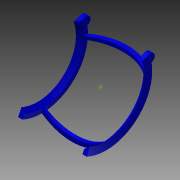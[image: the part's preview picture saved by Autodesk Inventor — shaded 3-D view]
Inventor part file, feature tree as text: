
AUTODESK INVENTOR PART (.ipt)
format: ipt  version: 2014 (Build 180170000, 170)  size: 196,608 bytes
history: native  units: in
note: dims shown in document units (in); Inventor stores cm internally (conversion verified against a paired STEP export)
features: sketch x8, revolve x4, extrude x3, plane x2, projected_geometry x2
ambient origin geometry x8: Origin, YZ Plane, XZ Plane, XY Plane, X Axis, Y Axis, Z Axis, Center Point
bodies: Solid1 (feature_tree)
feature tree (19):
  sketch  "Sketch1"  dims[d1=12.0in d3=12.0in]
  revolve  "Revolution1"  [1 undecoded]
  revolve  "Revolution2"  [1 undecoded]
  plane  "Work Plane1"
  plane  "Work Plane2"
  revolve  "Revolution4"  [1 undecoded]
  sketch  "Sketch6"  dims[d30=12.0in d31=12.0in]
  sketch  "3D Sketch2"
  sketch  "Sketch7"  dims[d32=0.0275in d33=0.5in]
  revolve  "Revolution5"  [1 undecoded]
  sketch  "Sketch8"  dims[d48=16.6756in d49=13.0in]
  extrude  "Extrusion1"  Depth=0.5in
  extrude  "Extrusion2"  Depth=13.0in
  extrude  "Extrusion3"  Depth=1.0in
  sketch  "Sketch2"  dims[d5=0.7559in d6=12.0in]
  projected_geometry  "Projected Loop1"
  sketch  "Sketch5"  dims[d8=0.0275in d9=12.0in]
  sketch  "Sketch9"  dims[d50=0.1718in d51=21.464in d52=1.0in d53=0.25in d54=1.0in d55=0.0in d56=1.0in d57=0.0in d58=1.0in d59=0.0in]
  projected_geometry  "Project Cut Edges2"
note: 4 required parameter values undecoded (feature->parameter linkage not recoverable at this tier; creation-order binding heuristic only, values carry confidence <= 0.55)
